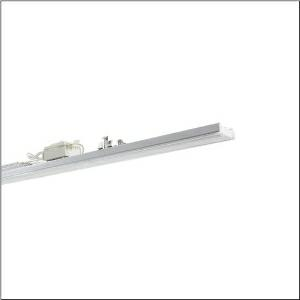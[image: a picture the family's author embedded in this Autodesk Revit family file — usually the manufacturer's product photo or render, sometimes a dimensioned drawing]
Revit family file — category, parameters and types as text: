
# Revit family: licross_r__21_recessed_ho_52tl1wdn4fxm_d124
name_source: partatom
category: Lighting Fixtures
units: mm (PartAtom-declared; Revit-internal decimal feet)

## family parameters
Cut with Voids When Loaded = No
Host = Face
Light Source = No
Part Type = Normal
Room Calculation Point = No
Round Connector Dimension = Use Diameter
Shared = No

## types (1)
- --- (1 x LED, 15050 lm, 84.6 W, 4000K)
    Apparent Load = 85 VA
    CIE Flux Codes = 73 94 99 100 100
    Color Rendering = 80
    Color Temperature = 4000K
    Default Elevation = 1800 mm
    Description = Licross® 21 Recessed HO, luminaire insert, of sheet steel, galvanised, coil coated, white, length: 1.500mm, width: 66mm, height: 67mm, LED rated luminous flux: 15.050lm, light colour: 840, control gear: DALI 2, with plug, 5-pole, with phase selection, mains connection: 220..240V, AC, 50/60Hz, rated input power: 85W, internal wiring halogen-free, primary optical cover: cover, of PMMA, light emission: direct distribution, primary light characteristic: symmetric, protection rating (complete): IP40, insulation class (complete): insulation class I (protective earthing), certification: CE, ENEC, VDE, UKCA, protection symbol: D if used in an environment without relevant dust loads with corresponding accessories, impact resistance: IK06, permissible ambient temperature for indoor applications: -25..+30°C, corresponds to IFS (International Featured Standards) requirements for safety and quality in the food industry, reducing of maximum allowable ambient temperature of 5°C with ceiling mounting, LABS conformity tested according to VDMA 24364:2018-05, packaging unit: 1 piece
    Height = 58 mm
    Lamp = 1 x LED
    Lamp Light Flux = 15050 lm
    Lamp Power = 84.6 W
    Lamp count = 1
    Length = 1500 mm
    Luminous efficacy = 178 lm/W
    Manufacturer = Siteco
    ModVariant = No
    Model = 52TL1WDN4FXM
    Mounting Place = Ceiling
    Mounting Type = Pendant
    Number of Poles = 1
    OnlyDefault = Yes
    Power Factor = 1
    Product Name = Licross® 21 Recessed HO
    Product group = luminaire insert | ceiling pendant
    ProductGroupID = 902
    Protection Class = Protection class I
    Protection Degree = IP 40
    RLX_Detail_Level = 1
    RLX_Emergency_Light_Flux = 0 lm
    RLX_Emergency_Type = 0
    RLX_Emergency_Type_DB = No
    RlxData = <blob elided: 24677 chars, md5=69d55f65>
    Socket = socket
    Standby Power = 0 W
    System Light Flux = 15050 lm
    System Power = 85 W
    Type Comments = factory setting: luminous flux: 100 % | dim-lin: 254 | 484 mA
    Type Image = l_1296930.jpg
    URL = http://relux.com
    VarID = @adj_080391
    Voltage = 0 V
    Weight = 0.00 kg
    Width = 66 mm

## geometry (parser evidence)
native form markers: Blend x4, Sweep x12
no freeform markers — native parametric forms only
